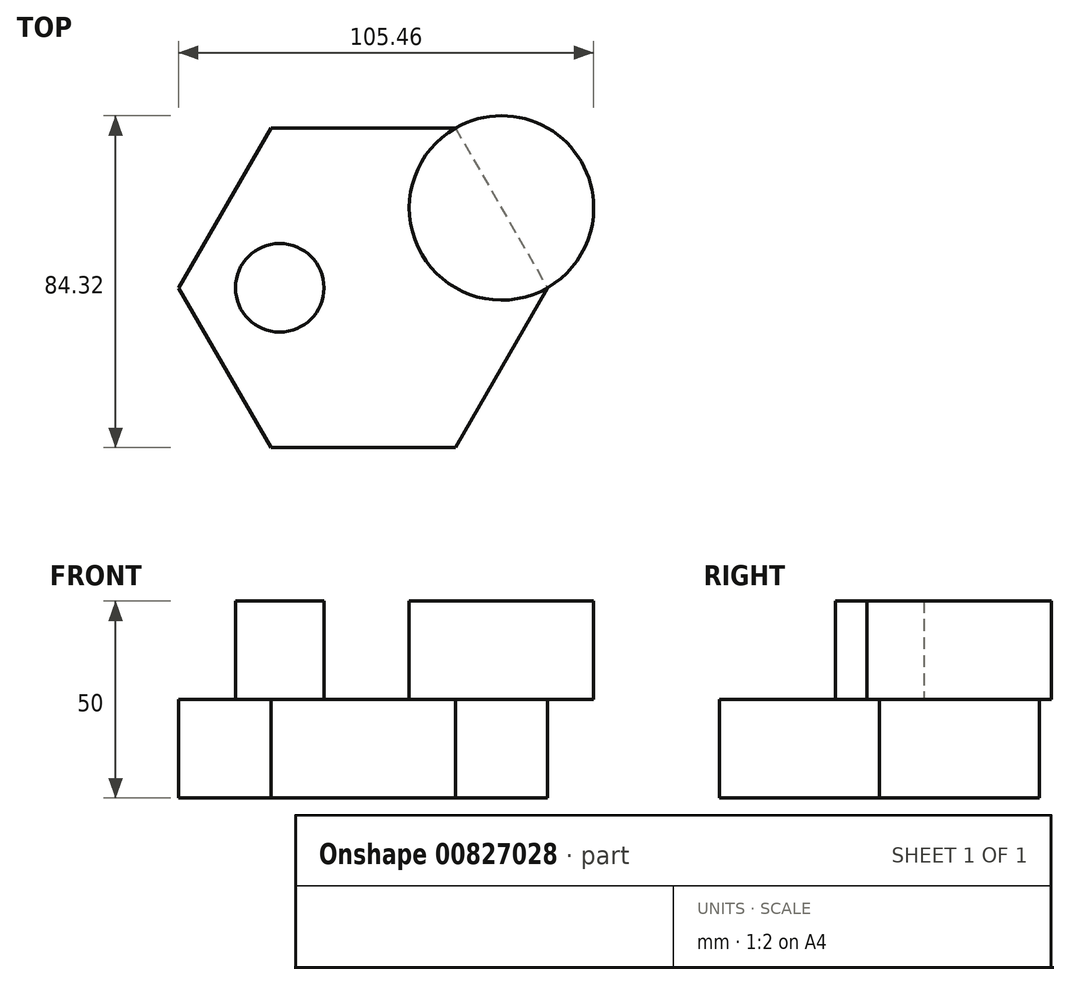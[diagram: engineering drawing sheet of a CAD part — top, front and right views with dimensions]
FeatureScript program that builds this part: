
annotation { "Feature Type Name" : "Feature", "Feature Type Description" : "" }
export const myFeature = defineFeature(function(context is Context, id is Id, definition is map)
    precondition{}
    {
        {
            var Q0;
            Q0=qCreatedBy(makeId("Top.planeOp"),FACE);
            var sketch = newSketch(context, id + "F0", { "sketchPlane" : qUnion([Q0])});
            skCircle(sketch, "E0.cCircle", {"center": v(0, 0) * mm, "radius": 40.59 * mm, "construction": true});
            skLineSegment(sketch, "E0.0", {"start": v(-23.43, 40.59) * mm, "end": v(23.43, 40.59) * mm});
            skLineSegment(sketch, "E0.1", {"start": v(23.43, 40.59) * mm, "end": v(46.87, 0) * mm});
            skLineSegment(sketch, "E0.2", {"start": v(46.87, 0) * mm, "end": v(23.43, -40.59) * mm});
            skLineSegment(sketch, "E0.3", {"start": v(23.43, -40.59) * mm, "end": v(-23.43, -40.59) * mm});
            skLineSegment(sketch, "E0.4", {"start": v(-23.43, -40.59) * mm, "end": v(-46.87, 0) * mm});
            skLineSegment(sketch, "E0.5", {"start": v(-46.87, 0) * mm, "end": v(-23.43, 40.59) * mm});
            skPoint(sketch, "E0.0.midPoint", {"position": v(0, 40.59) * mm});
            skSolve(sketch);
        }
        {
            var Q0;
            Q0=makeQuery(id+"F0.imprint","IMPRINT",FACE,{"disambiguationData":[TD([[makeQuery(id+"F0.imprint","IMPRINT",EDGE,{"derivedFrom":sQuery(id+"F0.wireOp",EDGE,"E0.0")}),-1.0]])]});
            extrude(context, id + "F1", {"entities" : qUnion([Q0]), "depth" : 25 * mm, "offsetDistance" : 25 * mm});
        }
        {
            var Q0;
            Q0=makeQuery(id+"F1.opExtrude","CAP_FACE",FACE,{"disambiguationData":[OSD([sQuery(id+"F0.wireOp",EDGE,"E0.0"),sQuery(id+"F0.wireOp",EDGE,"E0.1"),sQuery(id+"F0.wireOp",EDGE,"E0.2"),sQuery(id+"F0.wireOp",EDGE,"E0.3"),sQuery(id+"F0.wireOp",EDGE,"E0.4"),sQuery(id+"F0.wireOp",EDGE,"E0.5")])],"isStart":false});
            var sketch = newSketch(context, id + "F2", { "sketchPlane" : qUnion([Q0])});
            skCircle(sketch, "E1", {"center": v(35.15, 20.3) * mm, "radius": 23.43 * mm});
            skSolve(sketch);
        }
        {
            var Q0;
            {var subQ1=makeQuery(id+"F1.opExtrude","CAP_EDGE",EDGE,{"disambiguationData":[OSD([sQuery(id+"F0.wireOp",EDGE,"E0.1")])],"isStart":false});Q0=makeQuery(id+"F2.imprint","IMPRINT",FACE,{"disambiguationData":[TD([[makeQuery(id+"F2.imprint","IMPRINT",EDGE,{"derivedFrom":subQ1}),1.0]])]});}
            var Q1;
            {var subQ1=makeQuery(id+"F1.opExtrude","CAP_EDGE",EDGE,{"disambiguationData":[OSD([sQuery(id+"F0.wireOp",EDGE,"E0.1")])],"isStart":false});Q1=makeQuery(id+"F2.imprint","IMPRINT",FACE,{"disambiguationData":[TD([[makeQuery(id+"F2.imprint","IMPRINT",EDGE,{"derivedFrom":subQ1}),-1.0]])]});}
            extrude(context, id + "F3", {"entities" : qUnion([Q0, Q1]), "operationType" : NewBodyOperationType.ADD, "depth" : 25 * mm, "offsetDistance" : 25 * mm});
        }
        {
            var Q0;
            Q0=makeQuery(id+"F1.opExtrude","CAP_FACE",FACE,{"disambiguationData":[OSD([sQuery(id+"F0.wireOp",EDGE,"E0.0"),sQuery(id+"F0.wireOp",EDGE,"E0.1"),sQuery(id+"F0.wireOp",EDGE,"E0.2"),sQuery(id+"F0.wireOp",EDGE,"E0.3"),sQuery(id+"F0.wireOp",EDGE,"E0.4"),sQuery(id+"F0.wireOp",EDGE,"E0.5")])],"isStart":false});
            var sketch = newSketch(context, id + "F4", { "sketchPlane" : qUnion([Q0])});
            skCircle(sketch, "E2", {"center": v(-21.19, 0) * mm, "radius": 11.24 * mm});
            skSolve(sketch);
        }
        {
            var Q0;
            Q0=makeQuery(id+"F4.imprint","IMPRINT",FACE,{"disambiguationData":[TD([[makeQuery(id+"F4.imprint","IMPRINT",EDGE,{"derivedFrom":sQuery(id+"F4.wireOp",EDGE,"E2")}),1.0]])]});
            extrude(context, id + "F5", {"entities" : qUnion([Q0]), "operationType" : NewBodyOperationType.ADD, "depth" : 25 * mm, "offsetDistance" : 25 * mm});
        }
    });
